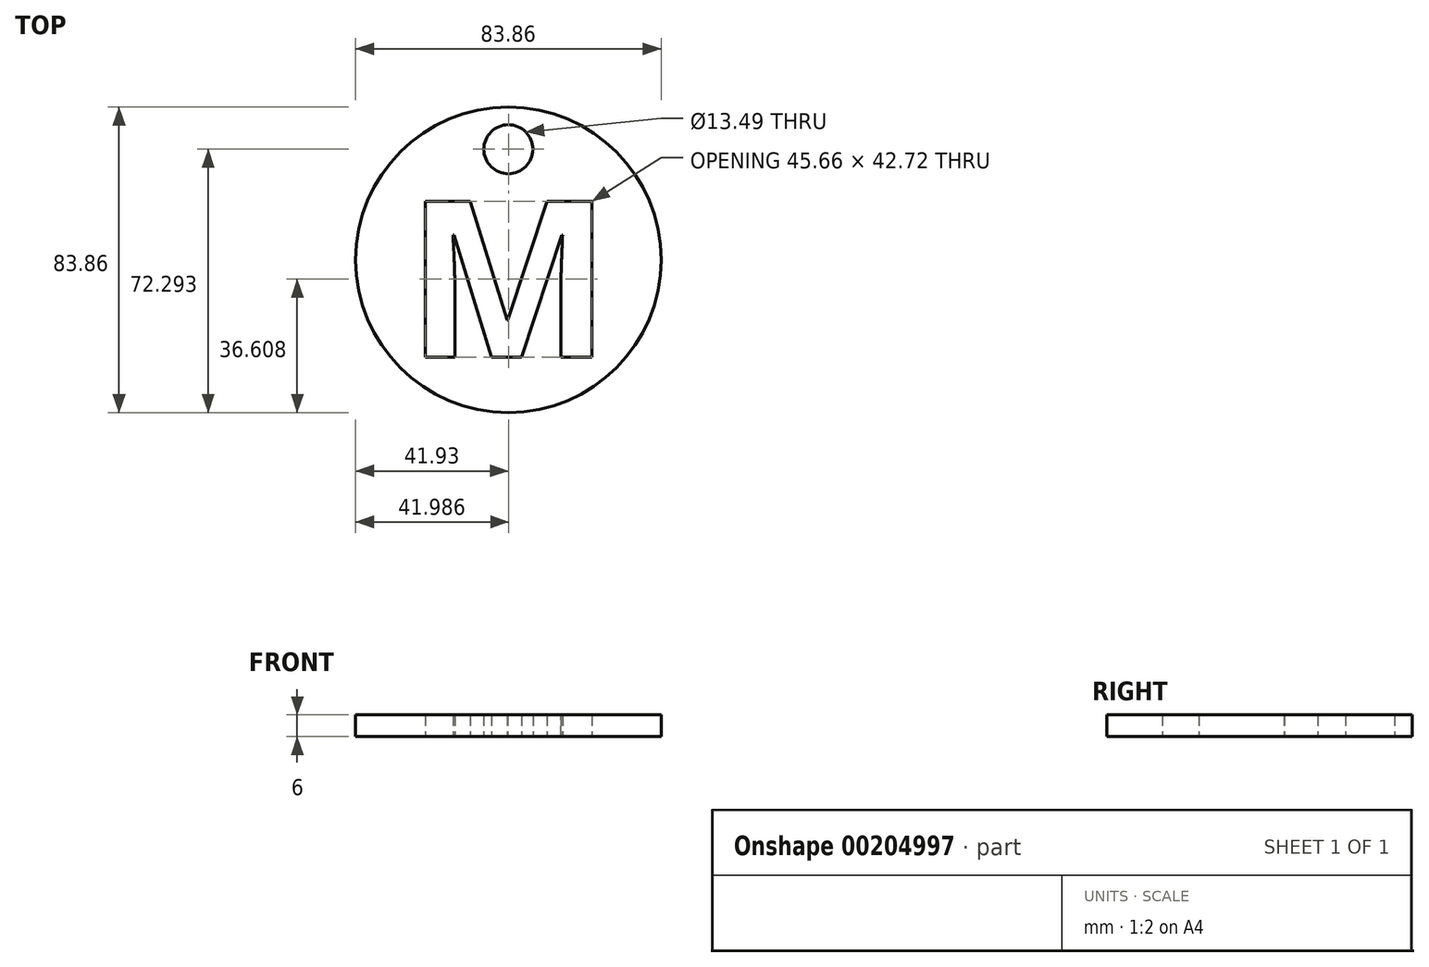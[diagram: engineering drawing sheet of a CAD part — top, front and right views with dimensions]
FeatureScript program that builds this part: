
annotation { "Feature Type Name" : "Feature", "Feature Type Description" : "" }
export const myFeature = defineFeature(function(context is Context, id is Id, definition is map)
    precondition{}
    {
        {
            var Q0;
            Q0=qCreatedBy(makeId("Top.planeOp"),FACE);
            var sketch = newSketch(context, id + "F0", { "sketchPlane" : qUnion([Q0])});
            skCircle(sketch, "E0", {"center": v(0, 0) * mm, "radius": 41.93 * mm});
            skSolve(sketch);
        }
        {
            var Q0;
            Q0 = qSketchRegion(id + "F0", true);
            extrude(context, id + "F1", {"entities" : qUnion([Q0]), "depth" : 6 * mm});
        }
        {
            var Q0;
            Q0=qCreatedBy(makeId("Top.planeOp"),FACE);
            var sketch = newSketch(context, id + "F2", { "sketchPlane" : qUnion([Q0])});
            skCircle(sketch, "E1", {"center": v(0, 30.36) * mm, "radius": 6.74 * mm});
            skSolve(sketch);
        }
        {
            var Q0;
            Q0 = qSketchRegion(id + "F2", true);
            extrude(context, id + "F3", {"entities" : qUnion([Q0]), "operationType" : NewBodyOperationType.REMOVE, "depth" : 71.2 * mm});
        }
        {
            var Q0;
            Q0=qCreatedBy(makeId("Top.planeOp"),FACE);
            var sketch = newSketch(context, id + "F4", { "sketchPlane" : qUnion([Q0])});
            skText(sketch, "E2", { "text": "M", "fontName": "OpenSans-Bold.ttf"});
            const initialGuessF4  = {"E2": [-0.02815, -0.02668, 1, 0, 0.04308]};
            skSetInitialGuess(sketch, initialGuessF4);
            skSolve(sketch);
        }
        {
            var Q0;
            Q0 = qSketchRegion(id + "F4", true);
            extrude(context, id + "F5", {"entities" : qUnion([Q0]), "operationType" : NewBodyOperationType.REMOVE, "depth" : 14.3 * mm});
        }
    });
